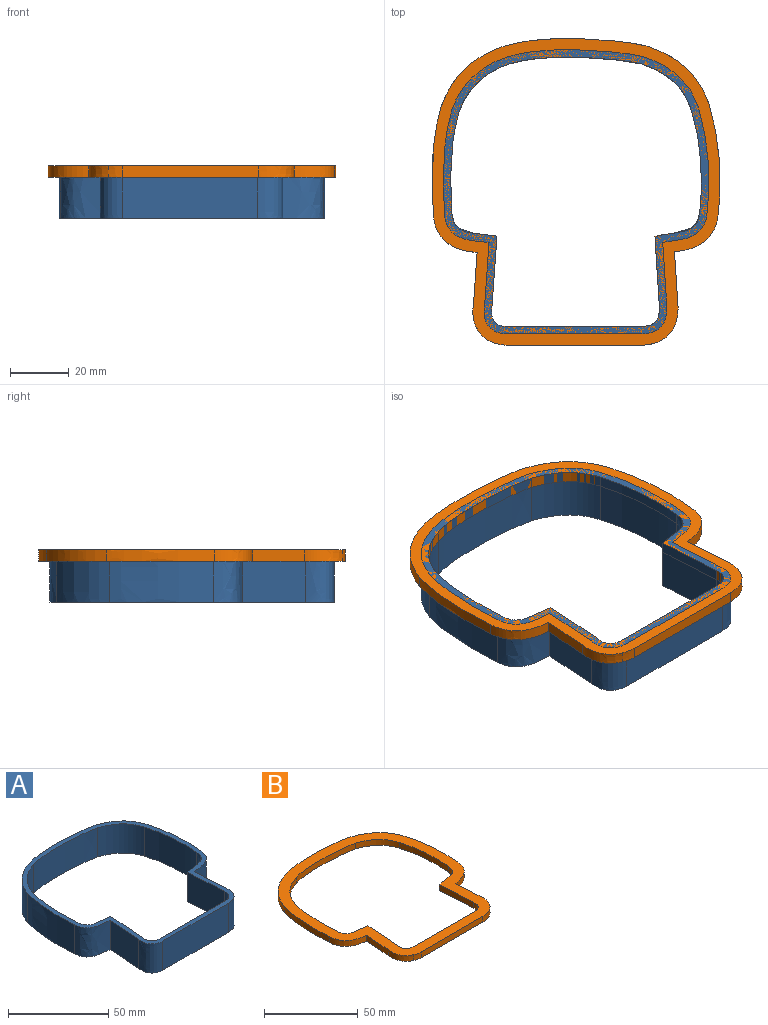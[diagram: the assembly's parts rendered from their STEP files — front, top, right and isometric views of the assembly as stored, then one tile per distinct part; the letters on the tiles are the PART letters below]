
ASSEMBLY  parts=2 mates=1
PART A: 26 faces, bbox 91x97.3x18.2 mm
  f0: plane 97.34x91.01mm, normal (0,0,1), area 824.1mm2, adj f2,f3,f4,f5,f6,f7,f8,f9
  f1: plane 97.34x91.01mm, normal (0,0,-1), area 824.1mm2, adj f2,f3,f4,f5,f6,f7,f8,f9
  f2: extruded ~17.78x15.2mm, area 362.1mm2, adj f0,f1,f3,f13
  f3: plane 21.48x17.78mm, normal (-1,0.07,0), area 382.9mm2, adj f0,f1,f2,f4
  f4: extruded ~17.78x9.7mm, area 252.3mm2, adj f0,f1,f3,f5
  f5: plane 46.24x17.78mm, normal (0,-1,0), area 822.1mm2, adj f0,f1,f4,f6
  f6: extruded ~17.78x8.82mm, area 247.6mm2, adj f0,f1,f5,f7
  f7: extruded ~22.44x17.78mm, area 399.9mm2, adj f0,f1,f6,f8
  f8: extruded ~17.78x15.16mm, area 366.5mm2, adj f0,f1,f7,f9
  f9: extruded ~35.02x17.78mm, area 628.8mm2, adj f0,f1,f8,f10
  f10: extruded ~18.76x17.84mm, area 480.1mm2, adj f0,f1,f9,f11
  f11: extruded ~46.48x17.78mm, area 832.8mm2, adj f0,f1,f10,f12
  f12: extruded ~19.02x18.09mm, area 485mm2, adj f0,f1,f11,f13
  f13: extruded ~35.42x17.78mm, area 634.6mm2, adj f0,f1,f2,f12
  f14: extruded ~17.78x15.37mm, area 342.6mm2, adj f0,f1,f15,f25
  f15: plane 23.98x17.78mm, normal (1,-0.07,0), area 427.4mm2, adj f0,f1,f14,f16
  f16: extruded ~17.78x6.87mm, area 177.5mm2, adj f0,f1,f15,f17
  f17: plane 46.1x17.78mm, normal (0,1,0), area 819.7mm2, adj f0,f1,f16,f18
  f18: extruded ~17.78x6.21mm, area 176.9mm2, adj f0,f1,f17,f19
  f19: extruded ~24.5x17.78mm, area 436.5mm2, adj f0,f1,f18,f20
  f20: extruded ~17.78x15.28mm, area 347.3mm2, adj f0,f1,f19,f21
  f21: extruded ~34.06x17.78mm, area 611.5mm2, adj f0,f1,f20,f22
  f22: extruded ~17.78x17.06mm, area 436.1mm2, adj f0,f1,f21,f23
  f23: extruded ~44.96x17.78mm, area 805.7mm2, adj f0,f1,f22,f24
  f24: extruded ~17.78x17.39mm, area 442.3mm2, adj f0,f1,f23,f25
  f25: extruded ~34.47x17.78mm, area 617.4mm2, adj f0,f1,f14,f24
PART B: 26 faces, bbox 99.9x106.2x5.4 mm
  f0: plane 106.2x99.86mm, normal (0,0,1), area 2127.5mm2, adj f2,f3,f4,f5,f6,f7,f8,f9
  f1: plane 106.2x99.86mm, normal (0,0,-1), area 2127.5mm2, adj f2,f3,f4,f5,f6,f7,f8,f9
  f2: extruded ~14.94x13.02mm, area 83.9mm2, adj f0,f1,f3,f13
  f3: plane 17.63x3.81mm, normal (-1,0.07,0), area 67.4mm2, adj f0,f1,f2,f4
  f4: extruded ~13.94x11.31mm, area 78.2mm2, adj f0,f1,f3,f5
  f5: plane 46.44x3.81mm, normal (0,-1,0), area 176.9mm2, adj f0,f1,f4,f6
  f6: extruded ~12.75x12.25mm, area 76.1mm2, adj f0,f1,f5,f7
  f7: extruded ~19.06x3.81mm, area 72.8mm2, adj f0,f1,f6,f8
  f8: extruded ~14.95x13.42mm, area 84.8mm2, adj f0,f1,f7,f9
  f9: extruded ~36.47x3.81mm, area 140.4mm2, adj f0,f1,f8,f10
  f10: extruded ~21.3x20.34mm, area 117mm2, adj f0,f1,f9,f11
  f11: extruded ~48.76x3.81mm, area 187.4mm2, adj f0,f1,f10,f12
  f12: extruded ~21.45x20.54mm, area 117.4mm2, adj f0,f1,f11,f13
  f13: extruded ~36.84x3.81mm, area 141.4mm2, adj f0,f1,f2,f12
  f14: extruded ~15.37x7.82mm, area 73.4mm2, adj f0,f1,f15,f25
  f15: plane 23.98x3.81mm, normal (1,-0.07,0), area 91.6mm2, adj f0,f1,f14,f16
  f16: extruded ~6.87x5.13mm, area 38mm2, adj f0,f1,f15,f17
  f17: plane 46.1x3.81mm, normal (0,1,0), area 175.7mm2, adj f0,f1,f16,f18
  f18: extruded ~6.21x6.07mm, area 37.9mm2, adj f0,f1,f17,f19
  f19: extruded ~24.5x3.81mm, area 93.5mm2, adj f0,f1,f18,f20
  f20: extruded ~15.28x8.65mm, area 74.4mm2, adj f0,f1,f19,f21
  f21: extruded ~34.06x3.81mm, area 131mm2, adj f0,f1,f20,f22
  f22: extruded ~17.06x16.17mm, area 93.4mm2, adj f0,f1,f21,f23
  f23: extruded ~44.96x3.81mm, area 172.7mm2, adj f0,f1,f22,f24
  f24: extruded ~17.39x16.46mm, area 94.8mm2, adj f0,f1,f23,f25
  f25: extruded ~34.47x3.81mm, area 132.3mm2, adj f0,f1,f14,f24
PLACE A t=(361.08,143.71,-15.88)mm
PLACE B t=(253.12,139.32,-1.91)mm
MATE fastened A.f0 <-> B.f0  axis (0,0,1) through (326.92,128.43,1.9)mm
